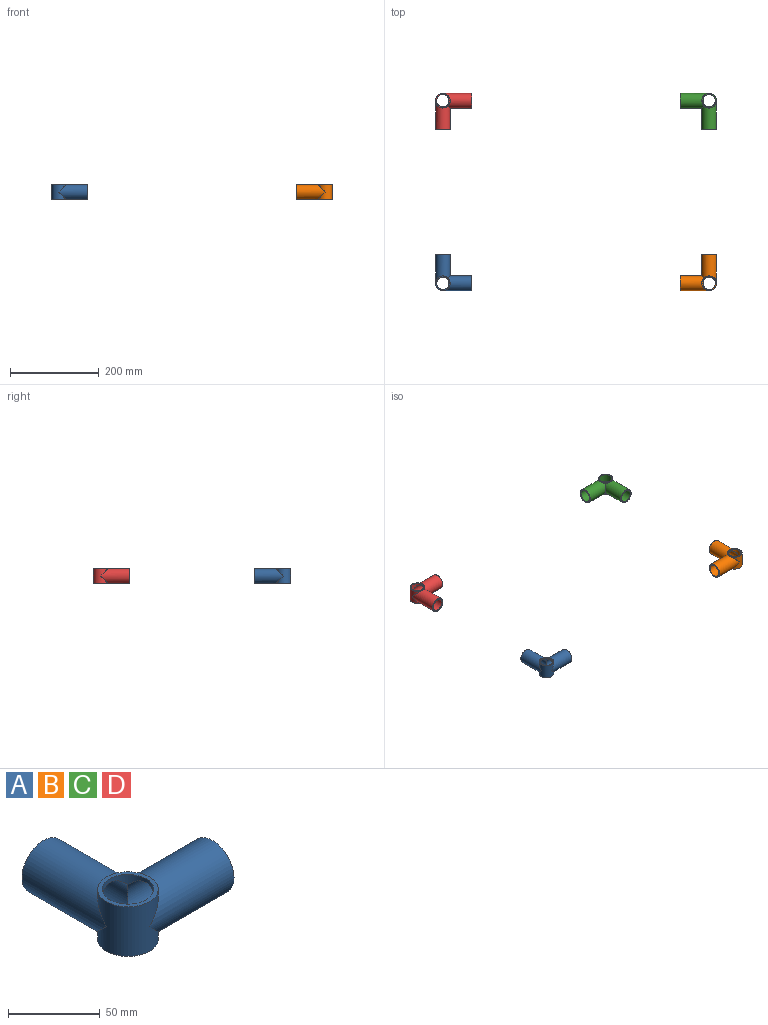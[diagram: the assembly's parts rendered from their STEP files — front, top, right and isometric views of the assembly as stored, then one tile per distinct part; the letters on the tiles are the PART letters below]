
ASSEMBLY  parts=4 mates=5
PART A: 12 faces, bbox 81.5x81.5x33 mm
  f0: plane 33x33mm, normal (0,0,1), area 239.5mm2, adj f3,f4,f10
  f1: plane 33x33mm, normal (1,0,0), area 239.5mm2, adj f2,f9
  f2: cylinder r=16.5mm len=65mm, axis (-1,0,0), area 5424.2mm2, adj f1,f3,f4,f5,f8
  f3: cylinder r=16.5mm len=33mm, axis (0,0,1), area 1476.9mm2, adj f0,f2,f6,f8
  f4: cylinder r=16.5mm len=16.5mm, axis (0,0,1), area 42.6mm2, adj f0,f2,f8
  f5: cylinder r=16.5mm len=16.5mm, axis (0,0,1), area 42.6mm2, adj f2,f6,f8
  f6: plane 33x33mm, normal (0,0,-1), area 239.5mm2, adj f3,f5,f10
  f7: plane 33x33mm, normal (0,1,0), area 239.5mm2, adj f8,f11
  f8: cylinder r=16.5mm len=65mm, axis (0,-1,0), area 5424.2mm2, adj f2,f3,f4,f5,f7
  f9: cylinder r=14mm len=65mm, axis (-1,0,0), area 4771.3mm2, adj f1,f10,f11
  f10: cylinder r=14mm len=33mm, axis (0,0,1), area 1564.5mm2, adj f0,f6,f9,f11
  f11: cylinder r=14mm len=65mm, axis (0,-1,0), area 4771.3mm2, adj f7,f9,f10
PART B: same geometry as A
PART C: same geometry as A
PART D: same geometry as A
PLACE A t=(-15.29,-18.71,0.55)mm fixed
PLACE B rot(axis=(0,0,1),90deg) t=(586.52,-18.71,0.55)mm
PLACE C rot(axis=(0,0,1),180deg) t=(586.52,393.83,0.55)mm
PLACE D rot(axis=(0,0,-1),90deg) t=(-15.29,393.83,0.55)mm
MATE cylindrical C.f2 <-> D.f8  axis (1,0,0) through (554.22,393.83,0.55)mm
MATE cylindrical A.f8 <-> D.f2  axis (0,-1,0) through (-15.29,46.29,0.55)mm
MATE cylindrical B.f8 <-> A.f2  axis (1,0,0) through (554.22,-18.71,0.55)mm
MATE cylindrical B.f2 <-> C.f8  axis (0,-1,0) through (586.52,13.6,0.55)mm
MATE parallel D.f3 <-> A.f3  axis (0,0,1) through (-15.29,393.83,17.05)mm
